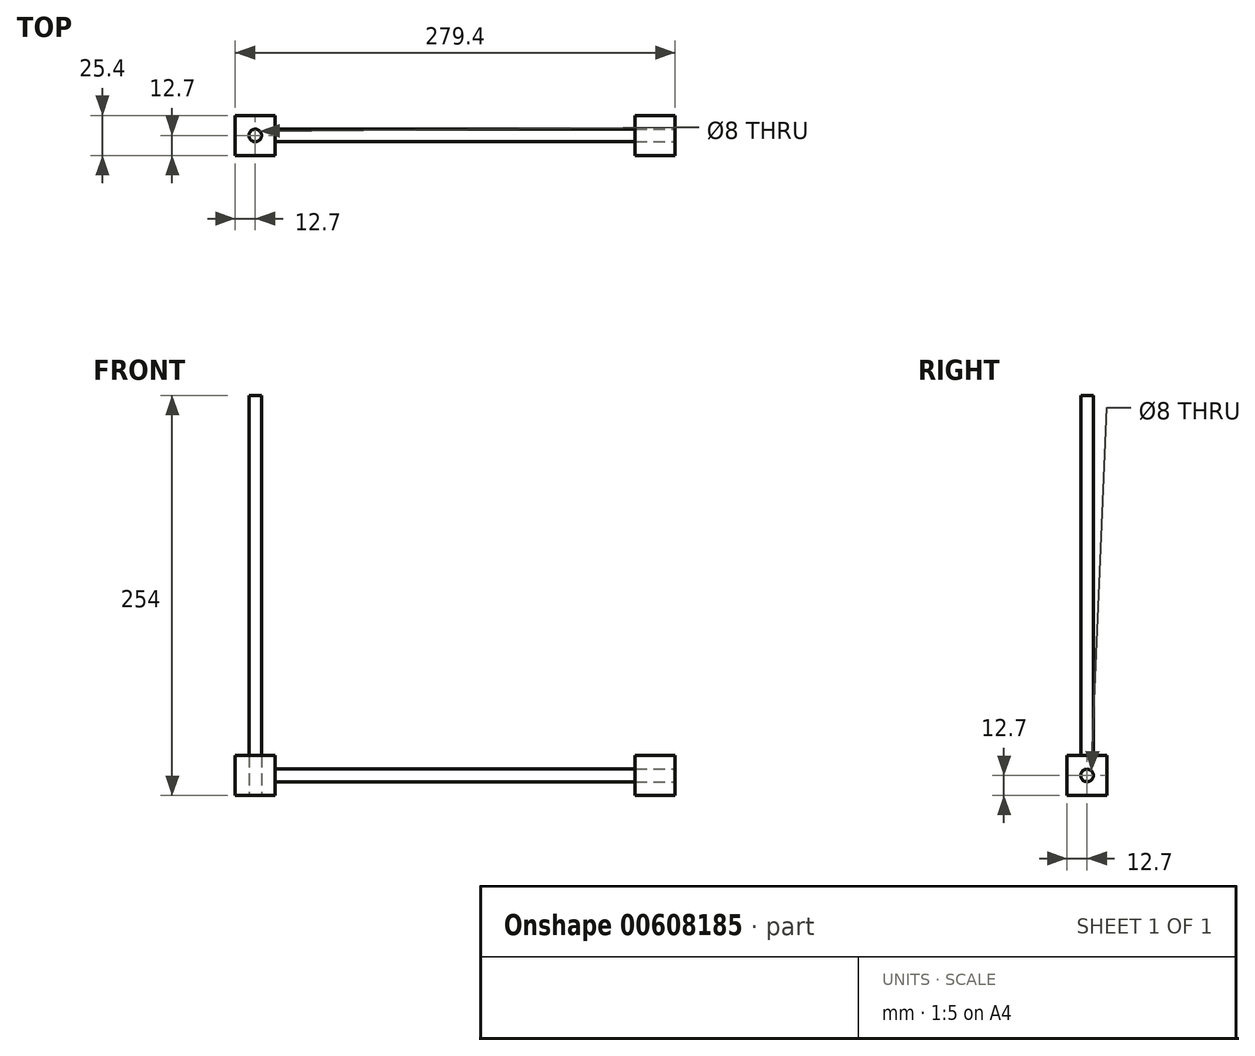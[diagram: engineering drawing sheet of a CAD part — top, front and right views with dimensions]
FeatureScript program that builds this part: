
annotation { "Feature Type Name" : "Feature", "Feature Type Description" : "" }
export const myFeature = defineFeature(function(context is Context, id is Id, definition is map)
    precondition{}
    {
        {
            var Q0;
            Q0=qCreatedBy(makeId("Top.planeOp"),FACE);
            var sketch = newSketch(context, id + "F0", { "sketchPlane" : qUnion([Q0])});
            skCircle(sketch, "E0", {"center": v(0, 0) * mm, "radius": 4 * mm});
            skSolve(sketch);
        }
        {
            var Q0;
            Q0 = qSketchRegion(id + "F0", true);
            var Q1;
            Q1=makeQuery(id+"F0.imprint","IMPRINT",FACE,{"disambiguationData":[TD([[makeQuery(id+"F0.imprint","IMPRINT",EDGE,{"derivedFrom":sQuery(id+"F0.wireOp",EDGE,"E0")}),1.0]])]});
            extrude(context, id + "F1", {"entities" : qUnion([Q0, Q1]), "depth" : 254 * mm, "offsetDistance" : 25.4 * mm});
        }
        {
            var Q0;
            Q0=qCreatedBy(makeId("Top.planeOp"),FACE);
            var sketch = newSketch(context, id + "F2", { "sketchPlane" : qUnion([Q0])});
            skLineSegment(sketch, "E1.bottom", {"start": v(-12.7, 12.7) * mm, "end": v(12.7, 12.7) * mm});
            skLineSegment(sketch, "E1.top", {"start": v(-12.7, -12.7) * mm, "end": v(12.7, -12.7) * mm});
            skLineSegment(sketch, "E1.left", {"start": v(-12.7, 12.7) * mm, "end": v(-12.7, -12.7) * mm});
            skLineSegment(sketch, "E1.right", {"start": v(12.7, 12.7) * mm, "end": v(12.7, -12.7) * mm});
            skCircle(sketch, "E2", {"center": v(0, 0) * mm, "radius": 4 * mm});
            skSolve(sketch);
        }
        {
            var Q0;
            Q0=makeQuery(id+"F2.imprint","IMPRINT",FACE,{"disambiguationData":[TD([[makeQuery(id+"F2.imprint","IMPRINT",EDGE,{"derivedFrom":sQuery(id+"F2.wireOp",EDGE,"E1.bottom")}),-1.0]])]});
            extrude(context, id + "F3", {"entities" : qUnion([Q0]), "depth" : 25.4 * mm, "offsetDistance" : 25.4 * mm});
        }
        {
            var Q0;
            Q0=makeQuery(id+"F3.opExtrude","SWEPT_FACE",FACE,{"disambiguationData":[OSD([sQuery(id+"F2.wireOp",EDGE,"E1.right")])]});
            var sketch = newSketch(context, id + "F4", { "sketchPlane" : qUnion([Q0])});
            skCircle(sketch, "E3", {"center": v(0, 12.7) * mm, "radius": 4 * mm});
            skPoint(sketch, "E3.centerSnap0", {"position": v(12.7, 12.7) * mm});
            skSolve(sketch);
        }
        {
            var Q0;
            Q0=makeQuery(id+"F4.imprint","IMPRINT",FACE,{"disambiguationData":[TD([[makeQuery(id+"F4.imprint","IMPRINT",EDGE,{"derivedFrom":sQuery(id+"F4.wireOp",EDGE,"E3")}),1.0]])]});
            extrude(context, id + "F5", {"entities" : qUnion([Q0]), "operationType" : NewBodyOperationType.ADD, "depth" : 254 * mm, "offsetDistance" : 25.4 * mm});
        }
        {
            var Q0;
            Q0=makeQuery(id+"F5.opExtrude","CAP_FACE",FACE,{"disambiguationData":[OSD([sQuery(id+"F4.wireOp",EDGE,"E3")])],"isStart":false});
            var sketch = newSketch(context, id + "F6", { "sketchPlane" : qUnion([Q0])});
            skCircle(sketch, "E4", {"center": v(0, 12.7) * mm, "radius": 4 * mm});
            skLineSegment(sketch, "E5.bottom", {"start": v(-12.7, 25.4) * mm, "end": v(12.7, 25.4) * mm});
            skLineSegment(sketch, "E5.top", {"start": v(-12.7, 0) * mm, "end": v(12.7, 0) * mm});
            skLineSegment(sketch, "E5.left", {"start": v(-12.7, 25.4) * mm, "end": v(-12.7, 0) * mm});
            skLineSegment(sketch, "E5.right", {"start": v(12.7, 25.4) * mm, "end": v(12.7, 0) * mm});
            skSolve(sketch);
        }
        {
            var Q0;
            Q0=makeQuery(id+"F6.imprint","IMPRINT",FACE,{"disambiguationData":[TD([[makeQuery(id+"F6.imprint","IMPRINT",EDGE,{"derivedFrom":sQuery(id+"F6.wireOp",EDGE,"E4")}),-1.0]])]});
            extrude(context, id + "F7", {"entities" : qUnion([Q0]), "oppositeDirection" : true, "depth" : 25.4 * mm, "offsetDistance" : 25.4 * mm});
        }
    });
